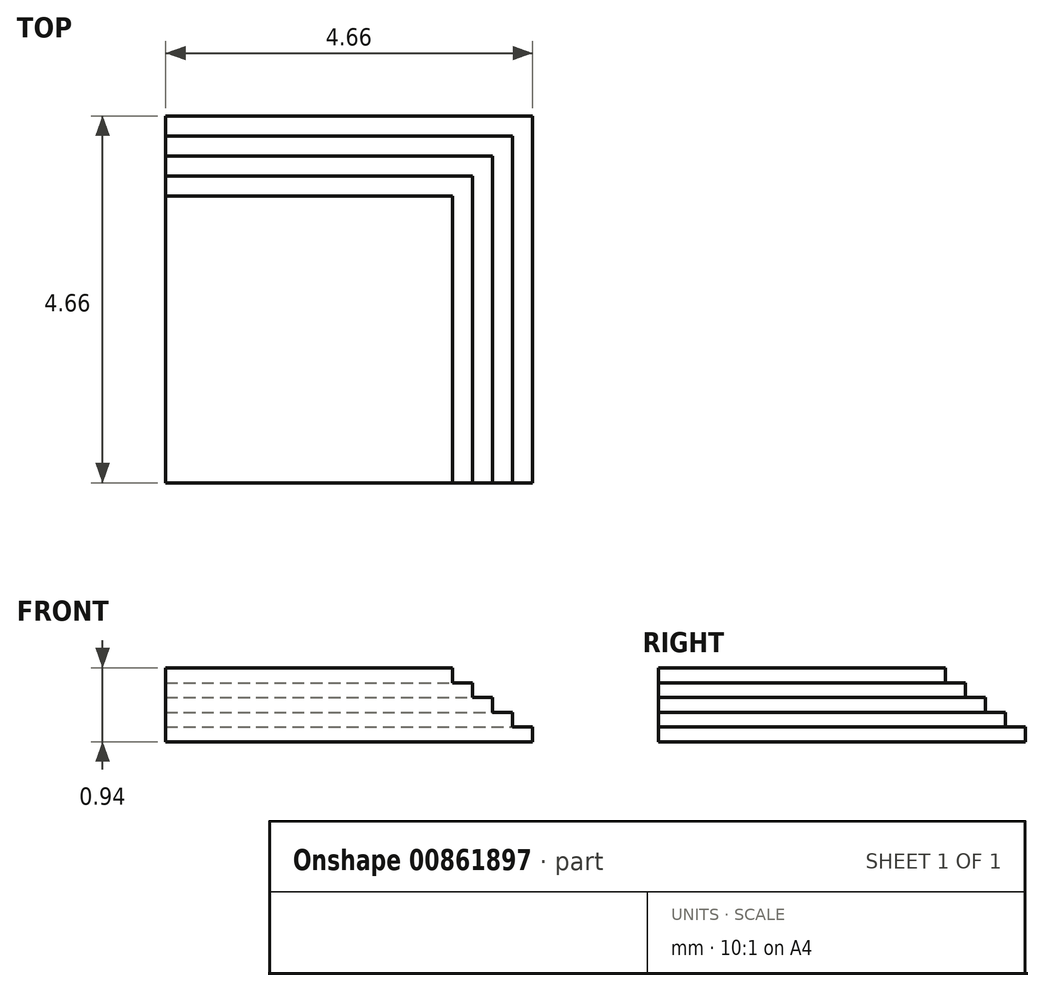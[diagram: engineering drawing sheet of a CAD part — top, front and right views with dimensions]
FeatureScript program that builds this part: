
annotation { "Feature Type Name" : "Feature", "Feature Type Description" : "" }
export const myFeature = defineFeature(function(context is Context, id is Id, definition is map)
    precondition{}
    {
        {
            assignVariable(context, id + "F0", {"name" : "D1", "anyValue" : 3 / 16});
        }
        {
            var Q0;
            Q0=qCreatedBy(makeId("Top.planeOp"),FACE);
            var sketch = newSketch(context, id + "F1", { "sketchPlane" : qUnion([Q0])});
            skLineSegment(sketch, "E0.bottom", {"start": v(0, 0) * mm, "end": v(4.66, 0) * mm});
            skLineSegment(sketch, "E0.top", {"start": v(0, 4.66) * mm, "end": v(4.66, 4.66) * mm});
            skLineSegment(sketch, "E0.left", {"start": v(0, 0) * mm, "end": v(0, 4.66) * mm});
            skLineSegment(sketch, "E0.right", {"start": v(4.66, 0) * mm, "end": v(4.66, 4.66) * mm});
            skSolve(sketch);
        }
        {
            var Q0;
            Q0=makeQuery(id+"F1.imprint","IMPRINT",FACE,{"disambiguationData":[TD([[makeQuery(id+"F1.imprint","IMPRINT",EDGE,{"derivedFrom":sQuery(id+"F1.wireOp",EDGE,"E0.bottom")}),1.0]])]});
            extrude(context, id + "F2", {"entities" : qUnion([Q0]), "depth" : (getVariable(context, 'D1')) * mm, "offsetDistance" : 25.4 * mm});
        }
        {
            var Q0;
            Q0=makeQuery(id+"F2.opExtrude","CAP_FACE",FACE,{"disambiguationData":[OSD([sQuery(id+"F1.wireOp",EDGE,"E0.bottom"),sQuery(id+"F1.wireOp",EDGE,"E0.top"),sQuery(id+"F1.wireOp",EDGE,"E0.left"),sQuery(id+"F1.wireOp",EDGE,"E0.right")])],"isStart":false});
            var sketch = newSketch(context, id + "F3", { "sketchPlane" : qUnion([Q0])});
            skLineSegment(sketch, "E1.bottom", {"start": v(0, 0) * mm, "end": v(4.4, 0) * mm});
            skLineSegment(sketch, "E1.top", {"start": v(0, 4.4) * mm, "end": v(4.4, 4.4) * mm});
            skLineSegment(sketch, "E1.left", {"start": v(0, 0) * mm, "end": v(0, 4.4) * mm});
            skLineSegment(sketch, "E1.right", {"start": v(4.4, 0) * mm, "end": v(4.4, 4.4) * mm});
            skSolve(sketch);
        }
        {
            var Q0;
            Q0=makeQuery(id+"F3.imprint","IMPRINT",FACE,{"disambiguationData":[TD([[makeQuery(id+"F3.imprint","IMPRINT",EDGE,{"derivedFrom":sQuery(id+"F3.wireOp",EDGE,"E1.bottom")}),1.0]])]});
            extrude(context, id + "F4", {"entities" : qUnion([Q0]), "operationType" : NewBodyOperationType.ADD, "depth" : (getVariable(context, 'D1')) * mm, "offsetDistance" : 25.4 * mm});
        }
        {
            var Q0;
            Q0=makeQuery(id+"F4.opExtrude","CAP_FACE",FACE,{"disambiguationData":[OSD([sQuery(id+"F3.wireOp",EDGE,"E1.bottom"),sQuery(id+"F3.wireOp",EDGE,"E1.top"),sQuery(id+"F3.wireOp",EDGE,"E1.left"),sQuery(id+"F3.wireOp",EDGE,"E1.right")])],"isStart":false});
            var sketch = newSketch(context, id + "F5", { "sketchPlane" : qUnion([Q0])});
            skLineSegment(sketch, "E2.bottom", {"start": v(0, 0) * mm, "end": v(4.15, 0) * mm});
            skLineSegment(sketch, "E2.top", {"start": v(0, 4.15) * mm, "end": v(4.15, 4.15) * mm});
            skLineSegment(sketch, "E2.left", {"start": v(0, 0) * mm, "end": v(0, 4.15) * mm});
            skLineSegment(sketch, "E2.right", {"start": v(4.15, 0) * mm, "end": v(4.15, 4.15) * mm});
            skSolve(sketch);
        }
        {
            var Q0;
            Q0=makeQuery(id+"F5.imprint","IMPRINT",FACE,{"disambiguationData":[TD([[makeQuery(id+"F5.imprint","IMPRINT",EDGE,{"derivedFrom":sQuery(id+"F5.wireOp",EDGE,"E2.bottom")}),1.0]])]});
            extrude(context, id + "F6", {"entities" : qUnion([Q0]), "operationType" : NewBodyOperationType.ADD, "depth" : (getVariable(context, 'D1')) * mm, "offsetDistance" : 25.4 * mm});
        }
        {
            var Q0;
            Q0=makeQuery(id+"F6.opExtrude","CAP_FACE",FACE,{"disambiguationData":[OSD([sQuery(id+"F5.wireOp",EDGE,"E2.bottom"),sQuery(id+"F5.wireOp",EDGE,"E2.top"),sQuery(id+"F5.wireOp",EDGE,"E2.left"),sQuery(id+"F5.wireOp",EDGE,"E2.right")])],"isStart":false});
            var sketch = newSketch(context, id + "F7", { "sketchPlane" : qUnion([Q0])});
            skLineSegment(sketch, "E3.bottom", {"start": v(0, 0) * mm, "end": v(3.9, 0) * mm});
            skLineSegment(sketch, "E3.top", {"start": v(0, 3.9) * mm, "end": v(3.9, 3.9) * mm});
            skLineSegment(sketch, "E3.left", {"start": v(0, 0) * mm, "end": v(0, 3.9) * mm});
            skLineSegment(sketch, "E3.right", {"start": v(3.9, 0) * mm, "end": v(3.9, 3.9) * mm});
            skSolve(sketch);
        }
        {
            var Q0;
            Q0 = qSketchRegion(id + "F7", true);
            extrude(context, id + "F8", {"entities" : qUnion([Q0]), "operationType" : NewBodyOperationType.ADD, "depth" : (getVariable(context, 'D1')) * mm, "offsetDistance" : 25.4 * mm});
        }
        {
            var Q0;
            Q0=makeQuery(id+"F8.opExtrude","CAP_FACE",FACE,{"disambiguationData":[OSD([sQuery(id+"F7.wireOp",EDGE,"E3.bottom"),sQuery(id+"F7.wireOp",EDGE,"E3.top"),sQuery(id+"F7.wireOp",EDGE,"E3.left"),sQuery(id+"F7.wireOp",EDGE,"E3.right")])],"isStart":false});
            var sketch = newSketch(context, id + "F9", { "sketchPlane" : qUnion([Q0])});
            skLineSegment(sketch, "E4.bottom", {"start": v(0, 0) * mm, "end": v(3.64, 0) * mm});
            skLineSegment(sketch, "E4.top", {"start": v(0, 3.64) * mm, "end": v(3.64, 3.64) * mm});
            skLineSegment(sketch, "E4.left", {"start": v(0, 0) * mm, "end": v(0, 3.64) * mm});
            skLineSegment(sketch, "E4.right", {"start": v(3.64, 0) * mm, "end": v(3.64, 3.64) * mm});
            skSolve(sketch);
        }
        {
            var Q0;
            Q0 = qSketchRegion(id + "F9", true);
            extrude(context, id + "F10", {"entities" : qUnion([Q0]), "operationType" : NewBodyOperationType.ADD, "depth" : (getVariable(context, 'D1')) * mm, "offsetDistance" : 25.4 * mm});
        }
    });
